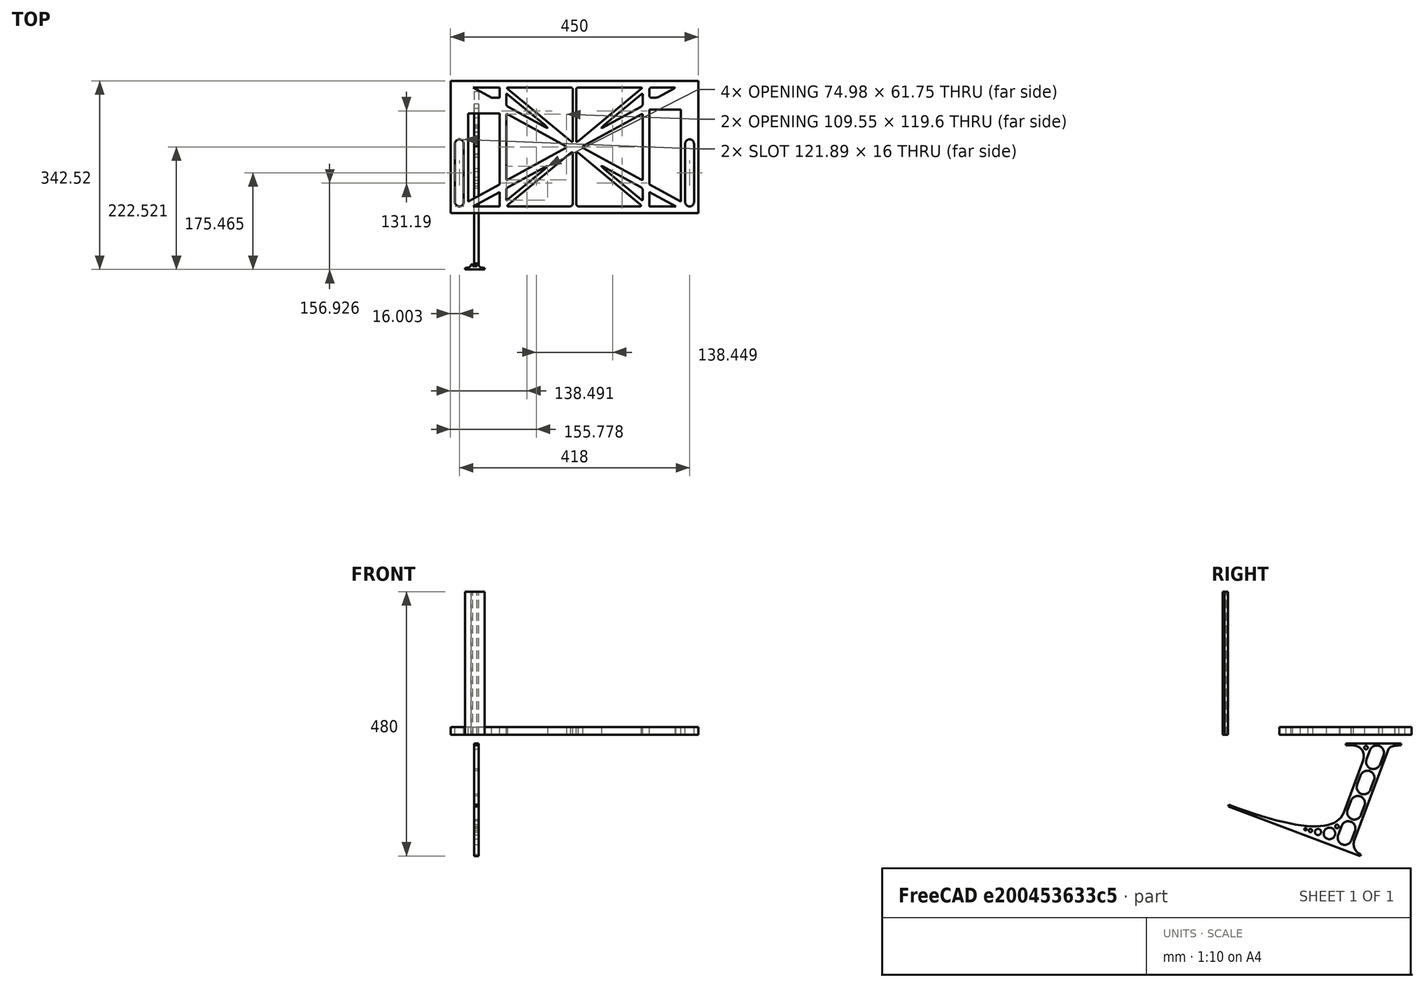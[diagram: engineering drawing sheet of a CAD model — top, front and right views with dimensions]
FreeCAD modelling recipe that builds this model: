
FCSTD DOCUMENT  (FreeCAD 0.19R0.19.2)
Label: laptopStand106
License: All rights reserved
LicenseURL: http://en.wikipedia.org/wiki/All_rights_reserved
objects: Sketcher::SketchObject×3, Part::Extrusion×3
note: 6 computed .brp shape members not serialized (recipe doc carries the construction recipe); baked Part::Feature solids carry a one-line shape summary decoded from their .brp

FEATURE [Sketcher::SketchObject] Sketch
  FullyConstrained = true
  sketch-geometry (288):
    g0: LineSegment StartX=-10.9272 StartY=-82.7794 StartZ=0 EndX=46.0728 EndY=-51.4823 EndZ=0
    g1: LineSegment StartX=366.073 StartY=-91.7794 StartZ=0 EndX=318.073 EndY=-65.424 EndZ=0
    g2: LineSegment StartX=-10.9272 StartY=77.3346 StartZ=0 EndX=-10.9272 EndY=-82.7794 EndZ=0
    g3: LineSegment StartX=-1.92719 StartY=-91.7794 StartZ=0 EndX=46.0728 EndY=-91.7794 EndZ=0
    g4: LineSegment StartX=318.073 StartY=-65.424 StartZ=0 EndX=318.073 EndY=-91.7794 EndZ=0
    g5: LineSegment StartX=318.073 StartY=-91.7794 StartZ=0 EndX=366.073 EndY=-91.7794 EndZ=0
    g6: LineSegment StartX=46.0728 StartY=-65.424 StartZ=0 EndX=-1.92719 EndY=-91.7794 EndZ=0
    g7: LineSegment StartX=46.0728 StartY=-65.424 StartZ=0 EndX=46.0728 EndY=-91.7794 EndZ=0
    g8: LineSegment StartX=46.0728 StartY=77.3346 StartZ=0 EndX=46.0728 EndY=-51.4823 EndZ=0
    g9: LineSegment StartX=-42.9272 StartY=136.221 StartZ=0 EndX=-42.9272 EndY=-103.779 EndZ=0
    g10: LineSegment StartX=407.073 StartY=136.221 StartZ=0 EndX=407.073 EndY=-103.779 EndZ=0
    g11: ArcOfCircle CenterX=-26.9272 CenterY=22.1087 CenterZ=0 NormalX=0 NormalY=0 NormalZ=1 AngleXU=0 Radius=8 StartAngle=1e-16 EndAngle=3.14159
    g12: ArcOfCircle CenterX=-26.9272 CenterY=-83.7794 CenterZ=0 NormalX=0 NormalY=0 NormalZ=1 AngleXU=0 Radius=8 StartAngle=3.14159 EndAngle=6.28319
    g13: LineSegment StartX=-34.9272 StartY=22.1087 StartZ=0 EndX=-34.9272 EndY=-83.7794 EndZ=0
    g14: LineSegment StartX=-18.9272 StartY=22.1087 StartZ=0 EndX=-18.9272 EndY=-83.7794 EndZ=0
    g15: ArcOfCircle CenterX=391.073 CenterY=22.1087 CenterZ=0 NormalX=0 NormalY=0 NormalZ=1 AngleXU=0 Radius=8 StartAngle=-4.4e-15 EndAngle=3.14159
    g16: LineSegment StartX=399.073 StartY=22.1087 StartZ=0 EndX=399.073 EndY=-83.7794 EndZ=0
    g17: LineSegment StartX=383.073 StartY=22.1087 StartZ=0 EndX=383.073 EndY=-83.7794 EndZ=0
    g18: ArcOfCircle CenterX=391.073 CenterY=-83.7794 CenterZ=0 NormalX=0 NormalY=0 NormalZ=1 AngleXU=0 Radius=8 StartAngle=3.14159 EndAngle=6.28319
    g19: Circle CenterX=175.022 CenterY=27.0628 CenterZ=0 NormalX=0 NormalY=0 NormalZ=1 AngleXU=0 Radius=1
    g20: Circle CenterX=179.022 CenterY=24.8665 CenterZ=0 NormalX=0 NormalY=0 NormalZ=1 AngleXU=0 Radius=1
    g21: Circle CenterX=179.022 CenterY=27.0628 CenterZ=0 NormalX=0 NormalY=0 NormalZ=1 AngleXU=0 Radius=1
    g22: BSplineCurve PolesCount=3 KnotsCount=2 Degree=2 IsPeriodic=0
    g23: GeomPoint X=175.022 Y=27.0628 Z=0
    g24: GeomPoint X=179.022 Y=27.0628 Z=0
    g25: Circle CenterX=189.124 CenterY=27.0628 CenterZ=0 NormalX=0 NormalY=0 NormalZ=1 AngleXU=0 Radius=1
    g26: Circle CenterX=185.124 CenterY=24.8665 CenterZ=0 NormalX=0 NormalY=0 NormalZ=1 AngleXU=0 Radius=1
    g27: Circle CenterX=185.124 CenterY=27.0628 CenterZ=0 NormalX=0 NormalY=0 NormalZ=1 AngleXU=0 Radius=1
    g28: BSplineCurve PolesCount=3 KnotsCount=2 Degree=2 IsPeriodic=0
    g29: GeomPoint X=189.124 Y=27.0628 Z=0
    g30: GeomPoint X=185.124 Y=27.0628 Z=0
    g31: Circle CenterX=175.022 CenterY=5.37834 CenterZ=0 NormalX=0 NormalY=0 NormalZ=1 AngleXU=0 Radius=1
    g32: Circle CenterX=179.022 CenterY=7.57463 CenterZ=0 NormalX=0 NormalY=0 NormalZ=1 AngleXU=0 Radius=1
    g33: Circle CenterX=179.022 CenterY=5.34704 CenterZ=0 NormalX=0 NormalY=0 NormalZ=1 AngleXU=0 Radius=1
    g34: BSplineCurve PolesCount=3 KnotsCount=2 Degree=2 IsPeriodic=0
    g35: GeomPoint X=175.022 Y=5.37834 Z=0
    g36: GeomPoint X=179.022 Y=5.34704 Z=0
    g37: Circle CenterX=189.124 CenterY=5.37834 CenterZ=0 NormalX=0 NormalY=0 NormalZ=1 AngleXU=0 Radius=1
    g38: Circle CenterX=185.124 CenterY=7.57463 CenterZ=0 NormalX=0 NormalY=0 NormalZ=1 AngleXU=0 Radius=1
    g39: Circle CenterX=185.124 CenterY=5.34704 CenterZ=0 NormalX=0 NormalY=0 NormalZ=1 AngleXU=0 Radius=1
    g40: BSplineCurve PolesCount=3 KnotsCount=2 Degree=2 IsPeriodic=0
    g41: GeomPoint X=189.124 Y=5.37834 Z=0
    g42: GeomPoint X=185.124 Y=5.34704 Z=0
    g43: Circle CenterX=165.871 CenterY=18.1458 CenterZ=0 NormalX=0 NormalY=0 NormalZ=1 AngleXU=0 Radius=1
    g44: Circle CenterX=169.377 CenterY=16.2206 CenterZ=0 NormalX=0 NormalY=0 NormalZ=1 AngleXU=0 Radius=1
    g45: Circle CenterX=165.871 CenterY=14.2954 CenterZ=0 NormalX=0 NormalY=0 NormalZ=1 AngleXU=0 Radius=1
    g46: BSplineCurve PolesCount=3 KnotsCount=2 Degree=2 IsPeriodic=0
    g47: GeomPoint X=165.871 Y=18.1458 Z=0
    g48: GeomPoint X=165.871 Y=14.2954 Z=0
    g49: Circle CenterX=198.275 CenterY=18.1458 CenterZ=0 NormalX=0 NormalY=0 NormalZ=1 AngleXU=0 Radius=1
    g50: Circle CenterX=194.768 CenterY=16.2206 CenterZ=0 NormalX=0 NormalY=0 NormalZ=1 AngleXU=0 Radius=1
    g51: Circle CenterX=198.275 CenterY=14.2954 CenterZ=0 NormalX=0 NormalY=0 NormalZ=1 AngleXU=0 Radius=1
    g52: BSplineCurve PolesCount=3 KnotsCount=2 Degree=2 IsPeriodic=0
    g53: GeomPoint X=198.275 Y=18.1458 Z=0
    g54: GeomPoint X=198.275 Y=14.2954 Z=0
    g55: LineSegment StartX=407.073 StartY=-103.779 StartZ=0 EndX=-42.9272 EndY=-103.779 EndZ=0
    g56: LineSegment StartX=407.073 StartY=136.221 StartZ=0 EndX=-42.9272 EndY=136.221 EndZ=0
    g57: LineSegment StartX=46.0728 StartY=77.3346 StartZ=0 EndX=-10.9272 EndY=77.3346 EndZ=0
    g58: LineSegment StartX=46.0728 StartY=105.865 StartZ=0 EndX=31.5028 EndY=105.865 EndZ=0
    g59: LineSegment StartX=46.0728 StartY=124.221 StartZ=0 EndX=46.0728 EndY=105.865 EndZ=0
    g60: LineSegment StartX=-1.92719 StartY=124.221 StartZ=0 EndX=31.5028 EndY=105.865 EndZ=0
    g61: LineSegment StartX=46.0728 StartY=124.221 StartZ=0 EndX=-1.92719 EndY=124.221 EndZ=0
    g62: Circle CenterX=125.607 CenterY=54.1951 CenterZ=0 NormalX=0 NormalY=0 NormalZ=1 AngleXU=0 Radius=1
    g63: Circle CenterX=139.632 CenterY=46.4944 CenterZ=0 NormalX=0 NormalY=0 NormalZ=1 AngleXU=0 Radius=1
    g64: Circle CenterX=127.326 CenterY=56.7187 CenterZ=0 NormalX=0 NormalY=0 NormalZ=1 AngleXU=0 Radius=1
    g65: BSplineCurve PolesCount=3 KnotsCount=2 Degree=2 IsPeriodic=0
    g66: GeomPoint X=125.607 Y=54.1951 Z=0
    g67: GeomPoint X=127.326 Y=56.7187 Z=0
    g68: Circle CenterX=236.821 CenterY=56.7187 CenterZ=0 NormalX=0 NormalY=0 NormalZ=1 AngleXU=0 Radius=1
    g69: Circle CenterX=224.513 CenterY=46.4944 CenterZ=0 NormalX=0 NormalY=0 NormalZ=1 AngleXU=0 Radius=1
    g70: Circle CenterX=238.538 CenterY=54.1951 CenterZ=0 NormalX=0 NormalY=0 NormalZ=1 AngleXU=0 Radius=1
    g71: BSplineCurve PolesCount=3 KnotsCount=2 Degree=2 IsPeriodic=0
    g72: GeomPoint X=236.821 Y=56.7187 Z=0
    g73: GeomPoint X=238.538 Y=54.1951 Z=0
    g74: Circle CenterX=238.538 CenterY=-21.7539 CenterZ=0 NormalX=0 NormalY=0 NormalZ=1 AngleXU=0 Radius=1
    g75: Circle CenterX=224.513 CenterY=-14.0532 CenterZ=0 NormalX=0 NormalY=0 NormalZ=1 AngleXU=0 Radius=1
    g76: Circle CenterX=236.821 CenterY=-24.2775 CenterZ=0 NormalX=0 NormalY=0 NormalZ=1 AngleXU=0 Radius=1
    g77: BSplineCurve PolesCount=3 KnotsCount=2 Degree=2 IsPeriodic=0
    g78: GeomPoint X=238.538 Y=-21.7539 Z=0
    g79: GeomPoint X=236.821 Y=-24.2775 Z=0
    g80: Circle CenterX=125.607 CenterY=-21.7539 CenterZ=0 NormalX=0 NormalY=0 NormalZ=1 AngleXU=0 Radius=1
    g81: Circle CenterX=139.632 CenterY=-14.0532 CenterZ=0 NormalX=0 NormalY=0 NormalZ=1 AngleXU=0 Radius=1
    g82: Circle CenterX=127.325 CenterY=-24.2775 CenterZ=0 NormalX=0 NormalY=0 NormalZ=1 AngleXU=0 Radius=1
    g83: BSplineCurve PolesCount=3 KnotsCount=2 Degree=2 IsPeriodic=0
    g84: GeomPoint X=125.607 Y=-21.7539 Z=0
    g85: GeomPoint X=127.325 Y=-24.2775 Z=0
    g86: Circle CenterX=302.996 CenterY=111.695 CenterZ=0 NormalX=0 NormalY=0 NormalZ=1 AngleXU=0 Radius=1
    g87: Circle CenterX=306.073 CenterY=114.251 CenterZ=0 NormalX=0 NormalY=0 NormalZ=1 AngleXU=0 Radius=1
    g88: Circle CenterX=306.073 CenterY=110.251 CenterZ=0 NormalX=0 NormalY=0 NormalZ=1 AngleXU=0 Radius=1
    g89: BSplineCurve PolesCount=3 KnotsCount=2 Degree=2 IsPeriodic=0
    g90: GeomPoint X=302.996 Y=111.695 Z=0
    g91: GeomPoint X=306.073 Y=110.251 Z=0
    g92: Circle CenterX=306.073 CenterY=95.2763 CenterZ=0 NormalX=0 NormalY=0 NormalZ=1 AngleXU=0 Radius=1
    g93: Circle CenterX=306.073 CenterY=91.2763 CenterZ=0 NormalX=0 NormalY=0 NormalZ=1 AngleXU=0 Radius=1
    g94: Circle CenterX=302.567 CenterY=89.3511 CenterZ=0 NormalX=0 NormalY=0 NormalZ=1 AngleXU=0 Radius=1
    g95: BSplineCurve PolesCount=3 KnotsCount=2 Degree=2 IsPeriodic=0
    g96: GeomPoint X=306.073 Y=95.2763 Z=0
    g97: GeomPoint X=302.567 Y=89.3511 Z=0
    g98: LineSegment StartX=306.073 StartY=110.251 StartZ=0 EndX=306.073 EndY=95.2763 EndZ=0
    g99: LineSegment StartX=302.996 StartY=111.695 StartZ=0 EndX=236.821 EndY=56.7187 EndZ=0
    g100: LineSegment StartX=238.538 StartY=54.1951 StartZ=0 EndX=302.567 EndY=89.3511 EndZ=0
    g101: Circle CenterX=61.1496 CenterY=111.695 CenterZ=0 NormalX=0 NormalY=0 NormalZ=1 AngleXU=0 Radius=1
    g102: Circle CenterX=58.0728 CenterY=114.251 CenterZ=0 NormalX=0 NormalY=0 NormalZ=1 AngleXU=0 Radius=1
    g103: Circle CenterX=58.0728 CenterY=110.251 CenterZ=0 NormalX=0 NormalY=0 NormalZ=1 AngleXU=0 Radius=1
    g104: BSplineCurve PolesCount=3 KnotsCount=2 Degree=2 IsPeriodic=0
    g105: GeomPoint X=61.1496 Y=111.695 Z=0
    g106: GeomPoint X=58.0728 Y=110.251 Z=0
    g107: Circle CenterX=61.5791 CenterY=89.3511 CenterZ=0 NormalX=0 NormalY=0 NormalZ=1 AngleXU=0 Radius=1
    g108: Circle CenterX=58.0728 CenterY=91.2763 CenterZ=0 NormalX=0 NormalY=0 NormalZ=1 AngleXU=0 Radius=1
    g109: Circle CenterX=58.0728 CenterY=95.2763 CenterZ=0 NormalX=0 NormalY=0 NormalZ=1 AngleXU=0 Radius=1
    g110: BSplineCurve PolesCount=3 KnotsCount=2 Degree=2 IsPeriodic=0
    g111: GeomPoint X=61.5791 Y=89.3511 Z=0
    g112: GeomPoint X=58.0728 Y=95.2763 Z=0
    g113: LineSegment StartX=58.0728 StartY=110.251 StartZ=0 EndX=58.0728 EndY=95.2763 EndZ=0
    g114: LineSegment StartX=61.1496 StartY=111.695 StartZ=0 EndX=127.326 EndY=56.7187 EndZ=0
    g115: LineSegment StartX=125.607 StartY=54.1951 StartZ=0 EndX=61.5791 EndY=89.3511 EndZ=0
    g116: Circle CenterX=61.5791 CenterY=-56.9099 CenterZ=0 NormalX=0 NormalY=0 NormalZ=1 AngleXU=0 Radius=1
    g117: Circle CenterX=58.0728 CenterY=-58.8351 CenterZ=0 NormalX=0 NormalY=0 NormalZ=1 AngleXU=0 Radius=1
    g118: Circle CenterX=58.0728 CenterY=-62.8351 CenterZ=0 NormalX=0 NormalY=0 NormalZ=1 AngleXU=0 Radius=1
    g119: BSplineCurve PolesCount=3 KnotsCount=2 Degree=2 IsPeriodic=0
    g120: GeomPoint X=61.5791 Y=-56.9099 Z=0
    g121: GeomPoint X=58.0728 Y=-62.8351 Z=0
    g122: Circle CenterX=58.0728 CenterY=-77.8102 CenterZ=0 NormalX=0 NormalY=0 NormalZ=1 AngleXU=0 Radius=1
    g123: Circle CenterX=58.0728 CenterY=-81.8102 CenterZ=0 NormalX=0 NormalY=0 NormalZ=1 AngleXU=0 Radius=1
    g124: Circle CenterX=61.1496 CenterY=-79.2541 CenterZ=0 NormalX=0 NormalY=0 NormalZ=1 AngleXU=0 Radius=1
    g125: BSplineCurve PolesCount=3 KnotsCount=2 Degree=2 IsPeriodic=0
    g126: GeomPoint X=58.0728 Y=-77.8102 Z=0
    g127: GeomPoint X=61.1496 Y=-79.2541 Z=0
    g128: LineSegment StartX=58.0728 StartY=-62.8351 StartZ=0 EndX=58.0728 EndY=-77.8102 EndZ=0
    g129: LineSegment StartX=61.1496 StartY=-79.2541 StartZ=0 EndX=127.325 EndY=-24.2775 EndZ=0
    g130: LineSegment StartX=125.607 StartY=-21.7539 StartZ=0 EndX=61.5791 EndY=-56.9099 EndZ=0
    g131: Circle CenterX=302.567 CenterY=-56.9099 CenterZ=0 NormalX=0 NormalY=0 NormalZ=1 AngleXU=0 Radius=1
    g132: Circle CenterX=306.073 CenterY=-58.8351 CenterZ=0 NormalX=0 NormalY=0 NormalZ=1 AngleXU=0 Radius=1
    g133: Circle CenterX=306.073 CenterY=-62.8351 CenterZ=0 NormalX=0 NormalY=0 NormalZ=1 AngleXU=0 Radius=1
    g134: BSplineCurve PolesCount=3 KnotsCount=2 Degree=2 IsPeriodic=0
    g135: GeomPoint X=302.567 Y=-56.9099 Z=0
    g136: GeomPoint X=306.073 Y=-62.8351 Z=0
    g137: Circle CenterX=302.996 CenterY=-79.2541 CenterZ=0 NormalX=0 NormalY=0 NormalZ=1 AngleXU=0 Radius=1
    g138: Circle CenterX=306.073 CenterY=-81.8102 CenterZ=0 NormalX=0 NormalY=0 NormalZ=1 AngleXU=0 Radius=1
    g139: Circle CenterX=306.073 CenterY=-77.8102 CenterZ=0 NormalX=0 NormalY=0 NormalZ=1 AngleXU=0 Radius=1
    g140: BSplineCurve PolesCount=3 KnotsCount=2 Degree=2 IsPeriodic=0
    g141: GeomPoint X=302.996 Y=-79.2541 Z=0
    g142: GeomPoint X=306.073 Y=-77.8102 Z=0
    g143: LineSegment StartX=306.073 StartY=-62.8351 StartZ=0 EndX=306.073 EndY=-77.8102 EndZ=0
    g144: LineSegment StartX=302.996 StartY=-79.2541 StartZ=0 EndX=236.821 EndY=-24.2775 EndZ=0
    g145: LineSegment StartX=238.538 StartY=-21.7539 StartZ=0 EndX=302.567 EndY=-56.9099 EndZ=0
    g146: Circle CenterX=61.6457 CenterY=-88.8112 CenterZ=0 NormalX=0 NormalY=0 NormalZ=1 AngleXU=0 Radius=1
    g147: Circle CenterX=58.0728 CenterY=-91.7794 CenterZ=0 NormalX=0 NormalY=0 NormalZ=1 AngleXU=0 Radius=1
    g148: Circle CenterX=63.9135 CenterY=-91.7794 CenterZ=0 NormalX=0 NormalY=0 NormalZ=1 AngleXU=0 Radius=1
    g149: BSplineCurve PolesCount=3 KnotsCount=2 Degree=2 IsPeriodic=0
    g150: GeomPoint X=61.6457 Y=-88.8112 Z=0
    g151: GeomPoint X=63.9135 Y=-91.7794 Z=0
    g152: Circle CenterX=179.022 CenterY=-85.8163 CenterZ=0 NormalX=0 NormalY=0 NormalZ=1 AngleXU=0 Radius=1
    g153: Circle CenterX=179.022 CenterY=-91.7794 CenterZ=0 NormalX=0 NormalY=0 NormalZ=1 AngleXU=0 Radius=1
    g154: Circle CenterX=171.895 CenterY=-91.7794 CenterZ=0 NormalX=0 NormalY=0 NormalZ=1 AngleXU=0 Radius=1
    g155: BSplineCurve PolesCount=3 KnotsCount=2 Degree=2 IsPeriodic=0
    g156: GeomPoint X=179.022 Y=-85.8163 Z=0
    g157: GeomPoint X=171.895 Y=-91.7794 Z=0
    g158: Circle CenterX=185.124 CenterY=-86.2028 CenterZ=0 NormalX=0 NormalY=0 NormalZ=1 AngleXU=0 Radius=1
    g159: Circle CenterX=185.124 CenterY=-91.7794 CenterZ=0 NormalX=0 NormalY=0 NormalZ=1 AngleXU=0 Radius=1
    g160: Circle CenterX=191.747 CenterY=-91.7794 CenterZ=0 NormalX=0 NormalY=0 NormalZ=1 AngleXU=0 Radius=1
    g161: BSplineCurve PolesCount=3 KnotsCount=2 Degree=2 IsPeriodic=0
    g162: GeomPoint X=185.124 Y=-86.2028 Z=0
    g163: GeomPoint X=191.747 Y=-91.7794 Z=0
    g164: Circle CenterX=299.888 CenterY=-86.6413 CenterZ=0 NormalX=0 NormalY=0 NormalZ=1 AngleXU=0 Radius=1
    g165: Circle CenterX=306.073 CenterY=-91.7794 CenterZ=0 NormalX=0 NormalY=0 NormalZ=1 AngleXU=0 Radius=1
    g166: Circle CenterX=298.776 CenterY=-91.7794 CenterZ=0 NormalX=0 NormalY=0 NormalZ=1 AngleXU=0 Radius=1
    g167: BSplineCurve PolesCount=3 KnotsCount=2 Degree=2 IsPeriodic=0
    g168: GeomPoint X=299.888 Y=-86.6413 Z=0
    g169: GeomPoint X=298.776 Y=-91.7794 Z=0
    g170: LineSegment StartX=189.124 StartY=5.37834 StartZ=0 EndX=299.888 EndY=-86.6413 EndZ=0
    g171: LineSegment StartX=298.776 StartY=-91.7794 StartZ=0 EndX=191.747 EndY=-91.7794 EndZ=0
    g172: LineSegment StartX=185.124 StartY=-86.2028 StartZ=0 EndX=185.124 EndY=5.34704 EndZ=0
    g173: LineSegment StartX=179.022 StartY=5.34704 StartZ=0 EndX=179.022 EndY=-85.8163 EndZ=0
    g174: LineSegment StartX=171.895 StartY=-91.7794 StartZ=0 EndX=63.9135 EndY=-91.7794 EndZ=0
    g175: LineSegment StartX=61.6457 StartY=-88.8112 StartZ=0 EndX=175.022 EndY=5.37834 EndZ=0
    g176: Circle CenterX=302.073 CenterY=124.221 CenterZ=0 NormalX=0 NormalY=0 NormalZ=1 AngleXU=0 Radius=1
    g177: Circle CenterX=306.073 CenterY=124.221 CenterZ=0 NormalX=0 NormalY=0 NormalZ=1 AngleXU=0 Radius=1
    g178: Circle CenterX=302.996 CenterY=121.665 CenterZ=0 NormalX=0 NormalY=0 NormalZ=1 AngleXU=0 Radius=1
    g179: BSplineCurve PolesCount=3 KnotsCount=2 Degree=2 IsPeriodic=0
    g180: GeomPoint X=302.073 Y=124.221 Z=0
    g181: GeomPoint X=302.996 Y=121.665 Z=0
    g182: Circle CenterX=189.124 CenterY=124.221 CenterZ=0 NormalX=0 NormalY=0 NormalZ=1 AngleXU=0 Radius=1
    g183: Circle CenterX=185.124 CenterY=124.221 CenterZ=0 NormalX=0 NormalY=0 NormalZ=1 AngleXU=0 Radius=1
    g184: Circle CenterX=185.124 CenterY=120.221 CenterZ=0 NormalX=0 NormalY=0 NormalZ=1 AngleXU=0 Radius=1
    g185: BSplineCurve PolesCount=3 KnotsCount=2 Degree=2 IsPeriodic=0
    g186: GeomPoint X=189.124 Y=124.221 Z=0
    g187: GeomPoint X=185.124 Y=120.221 Z=0
    g188: Circle CenterX=175.022 CenterY=124.221 CenterZ=0 NormalX=0 NormalY=0 NormalZ=1 AngleXU=0 Radius=1
    g189: Circle CenterX=179.022 CenterY=124.221 CenterZ=0 NormalX=0 NormalY=0 NormalZ=1 AngleXU=0 Radius=1
    g190: Circle CenterX=179.022 CenterY=120.221 CenterZ=0 NormalX=0 NormalY=0 NormalZ=1 AngleXU=0 Radius=1
    g191: BSplineCurve PolesCount=3 KnotsCount=2 Degree=2 IsPeriodic=0
    g192: GeomPoint X=175.022 Y=124.221 Z=0
    g193: GeomPoint X=179.022 Y=120.221 Z=0
    g194: Circle CenterX=62.0728 CenterY=124.221 CenterZ=0 NormalX=0 NormalY=0 NormalZ=1 AngleXU=0 Radius=1
    g195: Circle CenterX=58.0728 CenterY=124.221 CenterZ=0 NormalX=0 NormalY=0 NormalZ=1 AngleXU=0 Radius=1
    g196: Circle CenterX=61.1496 CenterY=121.665 CenterZ=0 NormalX=0 NormalY=0 NormalZ=1 AngleXU=0 Radius=1
    g197: BSplineCurve PolesCount=3 KnotsCount=2 Degree=2 IsPeriodic=0
    g198: GeomPoint X=62.0728 Y=124.221 Z=0
    g199: GeomPoint X=61.1496 Y=121.665 Z=0
    g200: LineSegment StartX=62.0728 StartY=124.221 StartZ=0 EndX=175.022 EndY=124.221 EndZ=0
    g201: LineSegment StartX=179.022 StartY=120.221 StartZ=0 EndX=179.022 EndY=27.0628 EndZ=0
    g202: LineSegment StartX=185.124 StartY=27.0628 StartZ=0 EndX=185.124 EndY=120.221 EndZ=0
    g203: LineSegment StartX=189.124 StartY=124.221 StartZ=0 EndX=302.073 EndY=124.221 EndZ=0
    g204: LineSegment StartX=302.996 StartY=121.665 StartZ=0 EndX=189.124 EndY=27.0628 EndZ=0
    g205: LineSegment StartX=175.022 StartY=27.0628 StartZ=0 EndX=61.1496 EndY=121.665 EndZ=0
    g206: Circle CenterX=61.5791 CenterY=75.4095 CenterZ=0 NormalX=0 NormalY=0 NormalZ=1 AngleXU=0 Radius=1
    g207: Circle CenterX=58.0728 CenterY=77.3346 CenterZ=0 NormalX=0 NormalY=0 NormalZ=1 AngleXU=0 Radius=1
    g208: Circle CenterX=58.0728 CenterY=73.3346 CenterZ=0 NormalX=0 NormalY=0 NormalZ=1 AngleXU=0 Radius=1
    g209: BSplineCurve PolesCount=3 KnotsCount=2 Degree=2 IsPeriodic=0
    g210: GeomPoint X=61.5791 Y=75.4095 Z=0
    g211: GeomPoint X=58.0728 Y=73.3346 Z=0
    g212: Circle CenterX=58.0728 CenterY=-40.8935 CenterZ=0 NormalX=0 NormalY=0 NormalZ=1 AngleXU=0 Radius=1
    g213: Circle CenterX=58.0728 CenterY=-44.8935 CenterZ=0 NormalX=0 NormalY=0 NormalZ=1 AngleXU=0 Radius=1
    g214: Circle CenterX=61.5791 CenterY=-42.9683 CenterZ=0 NormalX=0 NormalY=0 NormalZ=1 AngleXU=0 Radius=1
    g215: BSplineCurve PolesCount=3 KnotsCount=2 Degree=2 IsPeriodic=0
    g216: GeomPoint X=58.0728 Y=-40.8935 Z=0
    g217: GeomPoint X=61.5791 Y=-42.9683 Z=0
    g218: LineSegment StartX=61.5791 StartY=-42.9683 StartZ=0 EndX=165.871 EndY=14.2954 EndZ=0
    g219: LineSegment StartX=165.871 StartY=18.1458 StartZ=0 EndX=61.5791 EndY=75.4095 EndZ=0
    g220: LineSegment StartX=58.0728 StartY=73.3346 StartZ=0 EndX=58.0728 EndY=-40.8935 EndZ=0
    g221: Circle CenterX=302.567 CenterY=-42.9683 CenterZ=0 NormalX=0 NormalY=0 NormalZ=1 AngleXU=0 Radius=1
    g222: Circle CenterX=306.073 CenterY=-44.8935 CenterZ=0 NormalX=0 NormalY=0 NormalZ=1 AngleXU=0 Radius=1
    g223: Circle CenterX=306.073 CenterY=-40.8935 CenterZ=0 NormalX=0 NormalY=0 NormalZ=1 AngleXU=0 Radius=1
    g224: BSplineCurve PolesCount=3 KnotsCount=2 Degree=2 IsPeriodic=0
    g225: GeomPoint X=302.567 Y=-42.9683 Z=0
    g226: GeomPoint X=306.073 Y=-40.8935 Z=0
    g227: Circle CenterX=306.073 CenterY=73.3346 CenterZ=0 NormalX=0 NormalY=0 NormalZ=1 AngleXU=0 Radius=1
    g228: Circle CenterX=306.073 CenterY=77.3346 CenterZ=0 NormalX=0 NormalY=0 NormalZ=1 AngleXU=0 Radius=1
    g229: Circle CenterX=302.567 CenterY=75.4095 CenterZ=0 NormalX=0 NormalY=0 NormalZ=1 AngleXU=0 Radius=1
    g230: BSplineCurve PolesCount=3 KnotsCount=2 Degree=2 IsPeriodic=0
    g231: GeomPoint X=306.073 Y=73.3346 Z=0
    g232: GeomPoint X=302.567 Y=75.4095 Z=0
    g233: LineSegment StartX=302.567 StartY=-42.9683 StartZ=0 EndX=198.275 EndY=14.2954 EndZ=0
    g234: LineSegment StartX=198.275 StartY=18.1458 StartZ=0 EndX=302.567 EndY=75.4095 EndZ=0
    g235: LineSegment StartX=306.073 StartY=73.3346 StartZ=0 EndX=306.073 EndY=-40.8935 EndZ=0
    g236: LineSegment StartX=322.073 StartY=105.865 StartZ=0 EndX=328.643 EndY=105.865 EndZ=0
    g237: LineSegment StartX=318.073 StartY=120.221 StartZ=0 EndX=318.073 EndY=109.865 EndZ=0
    g238: LineSegment StartX=336.157 StartY=107.779 StartZ=0 EndX=362.567 EndY=122.294 EndZ=0
    g239: Circle CenterX=362.073 CenterY=124.221 CenterZ=0 NormalX=0 NormalY=0 NormalZ=1 AngleXU=0 Radius=1
    g240: Circle CenterX=366.073 CenterY=124.221 CenterZ=0 NormalX=0 NormalY=0 NormalZ=1 AngleXU=0 Radius=1
    g241: Circle CenterX=362.567 CenterY=122.294 CenterZ=0 NormalX=0 NormalY=0 NormalZ=1 AngleXU=0 Radius=1
    g242: BSplineCurve PolesCount=3 KnotsCount=2 Degree=2 IsPeriodic=0
    g243: GeomPoint X=362.073 Y=124.221 Z=0
    g244: GeomPoint X=362.567 Y=122.294 Z=0
    g245: Circle CenterX=322.073 CenterY=124.221 CenterZ=0 NormalX=0 NormalY=0 NormalZ=1 AngleXU=0 Radius=1
    g246: Circle CenterX=318.073 CenterY=124.221 CenterZ=0 NormalX=0 NormalY=0 NormalZ=1 AngleXU=0 Radius=1
    g247: Circle CenterX=318.073 CenterY=120.221 CenterZ=0 NormalX=0 NormalY=0 NormalZ=1 AngleXU=0 Radius=1
    g248: BSplineCurve PolesCount=3 KnotsCount=2 Degree=2 IsPeriodic=0
    g249: GeomPoint X=322.073 Y=124.221 Z=0
    g250: GeomPoint X=318.073 Y=120.221 Z=0
    g251: Circle CenterX=322.073 CenterY=105.865 CenterZ=0 NormalX=0 NormalY=0 NormalZ=1 AngleXU=0 Radius=1
    g252: Circle CenterX=318.073 CenterY=105.865 CenterZ=0 NormalX=0 NormalY=0 NormalZ=1 AngleXU=0 Radius=1
    g253: Circle CenterX=318.073 CenterY=109.865 CenterZ=0 NormalX=0 NormalY=0 NormalZ=1 AngleXU=0 Radius=1
    g254: BSplineCurve PolesCount=3 KnotsCount=2 Degree=2 IsPeriodic=0
    g255: GeomPoint X=322.073 Y=105.865 Z=0
    g256: GeomPoint X=318.073 Y=109.865 Z=0
    g257: Circle CenterX=336.157 CenterY=107.779 CenterZ=0 NormalX=0 NormalY=0 NormalZ=1 AngleXU=0 Radius=1
    g258: Circle CenterX=332.651 CenterY=105.853 CenterZ=0 NormalX=0 NormalY=0 NormalZ=1 AngleXU=0 Radius=1
    g259: Circle CenterX=328.643 CenterY=105.865 CenterZ=0 NormalX=0 NormalY=0 NormalZ=1 AngleXU=0 Radius=1
    g260: BSplineCurve PolesCount=3 KnotsCount=2 Degree=2 IsPeriodic=0
    g261: GeomPoint X=336.157 Y=107.779 Z=0
    g262: GeomPoint X=328.643 Y=105.865 Z=0
    g263: LineSegment StartX=322.073 StartY=124.221 StartZ=0 EndX=362.073 EndY=124.221 EndZ=0
    g264: Circle CenterX=371.567 CenterY=-80.8644 CenterZ=0 NormalX=0 NormalY=0 NormalZ=1 AngleXU=0 Radius=1
    g265: Circle CenterX=375.073 CenterY=-82.7896 CenterZ=0 NormalX=0 NormalY=0 NormalZ=1 AngleXU=0 Radius=1
    g266: Circle CenterX=375.073 CenterY=-78.7896 CenterZ=0 NormalX=0 NormalY=0 NormalZ=1 AngleXU=0 Radius=1
    g267: BSplineCurve PolesCount=3 KnotsCount=2 Degree=2 IsPeriodic=0
    g268: GeomPoint X=371.567 Y=-80.8644 Z=0
    g269: GeomPoint X=375.073 Y=-78.7896 Z=0
    g270: Circle CenterX=321.579 CenterY=-53.4075 CenterZ=0 NormalX=0 NormalY=0 NormalZ=1 AngleXU=0 Radius=1
    g271: Circle CenterX=318.073 CenterY=-51.4823 CenterZ=0 NormalX=0 NormalY=0 NormalZ=1 AngleXU=0 Radius=1
    g272: Circle CenterX=318.073 CenterY=-47.4823 CenterZ=0 NormalX=0 NormalY=0 NormalZ=1 AngleXU=0 Radius=1
    g273: BSplineCurve PolesCount=3 KnotsCount=2 Degree=2 IsPeriodic=0
    g274: GeomPoint X=321.579 Y=-53.4075 Z=0
    g275: GeomPoint X=318.073 Y=-47.4823 Z=0
    g276: Circle CenterX=318.073 CenterY=79.9235 CenterZ=0 NormalX=0 NormalY=0 NormalZ=1 AngleXU=0 Radius=1
    g277: Circle CenterX=318.073 CenterY=83.9235 CenterZ=0 NormalX=0 NormalY=0 NormalZ=1 AngleXU=0 Radius=1
    g278: Circle CenterX=322.073 CenterY=83.9235 CenterZ=0 NormalX=0 NormalY=0 NormalZ=1 AngleXU=0 Radius=1
    g279: BSplineCurve PolesCount=3 KnotsCount=2 Degree=2 IsPeriodic=0
    g280: GeomPoint X=318.073 Y=79.9235 Z=0
    g281: GeomPoint X=322.073 Y=83.9235 Z=0
    g282: Circle CenterX=375.073 CenterY=79.9235 CenterZ=0 NormalX=0 NormalY=0 NormalZ=1 AngleXU=0 Radius=1
    g283: Circle CenterX=375.073 CenterY=83.9235 CenterZ=0 NormalX=0 NormalY=0 NormalZ=1 AngleXU=0 Radius=1
    g284: Circle CenterX=371.073 CenterY=83.9235 CenterZ=0 NormalX=0 NormalY=0 NormalZ=1 AngleXU=0 Radius=1
    g285: BSplineCurve PolesCount=3 KnotsCount=2 Degree=2 IsPeriodic=0
    g286: GeomPoint X=375.073 Y=79.9235 Z=0
    g287: GeomPoint X=371.073 Y=83.9235 Z=0
  constraints (477):
    c: Horizontal(g3)
    c: Coincident(g4,g1)
    c: Coincident(g7,g6)
    c: Coincident(g0,g8)
    c: Block(g1)
    c: Block(g4)
    c: Block(g7)
    c: Block(g6)
    c: Block(g0)
    c: Block(g2)
    c: Block(g5)
    c: Block(g3)
    c: Vertical(g9)
    c: Vertical(g10)
    c: Block(g10)
    c: Block(g9)
    c: Tangent(g11,g14) = 1.5708
    c: Tangent(g11,g13) = -1.5708
    c: Tangent(g13,g12) = -1.5708
    c: Tangent(g14,g12) = 1.5708
    c: Vertical(g13)
    c: Equal(g11,g12)
    c: Block(g14)
    c: Block(g13)
    c: Tangent(g15,g16) = 1.5708
    c: Tangent(g16,g18) = 1.5708
    c: Equal(g15,g18)
    c: Coincident(g17,g15)
    c: Coincident(g17,g18)
    c: Block(g16)
    c: Block(g17)
    c: Weight(g19) = 1
    c: Equal(g19,g20)
    c: Equal(g19,g21)
    c: InternalAlignment(g19,g22)
    c: InternalAlignment(g20,g22)
    c: InternalAlignment(g21,g22)
    c: InternalAlignment(g23,g22)
    c: InternalAlignment(g24,g22)
    c: Weight(g25) = 1
    c: Equal(g25,g26)
    c: Equal(g25,g27)
    c: InternalAlignment(g25,g28)
    c: InternalAlignment(g26,g28)
    c: InternalAlignment(g27,g28)
    c: InternalAlignment(g29,g28)
    c: InternalAlignment(g30,g28)
    c: Block(g28)
    c: Block(g22)
    c: Weight(g31) = 1
    c: Equal(g31,g32)
    c: Equal(g31,g33)
    c: InternalAlignment(g31,g34)
    c: InternalAlignment(g32,g34)
    c: InternalAlignment(g33,g34)
    c: InternalAlignment(g35,g34)
    c: InternalAlignment(g36,g34)
    c: Weight(g37) = 1
    c: Equal(g37,g38)
    c: Equal(g37,g39)
    c: InternalAlignment(g37,g40)
    c: InternalAlignment(g38,g40)
    c: InternalAlignment(g39,g40)
    c: InternalAlignment(g41,g40)
    c: InternalAlignment(g42,g40)
    c: Block(g40)
    c: Block(g34)
    c: Weight(g43) = 1
    c: Equal(g43,g44)
    c: Equal(g43,g45)
    c: InternalAlignment(g43,g46)
    c: InternalAlignment(g44,g46)
    c: InternalAlignment(g45,g46)
    c: InternalAlignment(g47,g46)
    c: InternalAlignment(g48,g46)
    c: Weight(g49) = 1
    c: Equal(g49,g50)
    c: Equal(g49,g51)
    c: InternalAlignment(g49,g52)
    c: InternalAlignment(g50,g52)
    c: InternalAlignment(g51,g52)
    c: InternalAlignment(g53,g52)
    c: InternalAlignment(g54,g52)
    c: Block(g46)
    c: Block(g52)
    c: Coincident(g55,g10)
    c: Coincident(g55,g9)
    c: Horizontal(g55)
    c: Distance(g55) = 450
    c: Coincident(g56,g10)
    c: Coincident(g56,g9)
    c: Horizontal(g56)
    c: Horizontal(g57)
    c: Coincident(g8,g57)
    c: Horizontal(g58)
    c: Vertical(g59)
    c: Block(g59)
    c: Block(g58)
    c: Block(g57)
    c: Distance(g59) = 18.3554
    c: Coincident(g61,g59)
    c: Coincident(g61,g60)
    c: Horizontal(g61)
    c: Block(g61)
    c: Block(g60)
    c: Coincident(g58,g60)
    c: Coincident(g2,g57)
    c: Weight(g62) = 1
    c: Equal(g62,g63)
    c: Equal(g62,g64)
    c: InternalAlignment(g62,g65)
    c: InternalAlignment(g63,g65)
    c: InternalAlignment(g64,g65)
    c: InternalAlignment(g66,g65)
    c: InternalAlignment(g67,g65)
    c: Block(g65)
    c: Weight(g68) = 1
    c: Equal(g68,g69)
    c: Equal(g68,g70)
    c: InternalAlignment(g68,g71)
    c: InternalAlignment(g69,g71)
    c: InternalAlignment(g70,g71)
    c: InternalAlignment(g72,g71)
    c: InternalAlignment(g73,g71)
    c: Block(g71)
    c: Weight(g74) = 1
    c: Equal(g74,g75)
    c: Equal(g74,g76)
    c: InternalAlignment(g74,g77)
    c: InternalAlignment(g75,g77)
    c: InternalAlignment(g76,g77)
    c: InternalAlignment(g78,g77)
    c: InternalAlignment(g79,g77)
    c: Block(g77)
    c: Weight(g80) = 1
    c: Equal(g80,g81)
    c: Equal(g80,g82)
    c: InternalAlignment(g80,g83)
    c: InternalAlignment(g81,g83)
    c: InternalAlignment(g82,g83)
    c: InternalAlignment(g84,g83)
    c: InternalAlignment(g85,g83)
    c: Block(g83)
    c: Weight(g86) = 1
    c: Equal(g86,g87)
    c: Equal(g86,g88)
    c: InternalAlignment(g86,g89)
    c: InternalAlignment(g87,g89)
    c: InternalAlignment(g88,g89)
    c: InternalAlignment(g90,g89)
    c: InternalAlignment(g91,g89)
    c: Weight(g92) = 1
    c: Equal(g92,g93)
    c: Equal(g92,g94)
    c: InternalAlignment(g92,g95)
    c: InternalAlignment(g93,g95)
    c: InternalAlignment(g94,g95)
    c: InternalAlignment(g96,g95)
    c: InternalAlignment(g97,g95)
    c: Block(g89)
    c: Block(g95)
    c: Coincident(g98,g89)
    c: Coincident(g98,g95)
    c: Vertical(g98)
    c: Coincident(g99,g89)
    c: Coincident(g99,g71)
    c: Coincident(g100,g71)
    c: Coincident(g100,g95)
    c: Weight(g101) = 1
    c: Equal(g101,g102)
    c: Equal(g101,g103)
    c: InternalAlignment(g101,g104)
    c: InternalAlignment(g102,g104)
    c: InternalAlignment(g103,g104)
    c: InternalAlignment(g105,g104)
    c: InternalAlignment(g106,g104)
    c: Weight(g107) = 1
    c: Equal(g107,g108)
    c: Equal(g107,g109)
    c: InternalAlignment(g107,g110)
    c: InternalAlignment(g108,g110)
    c: InternalAlignment(g109,g110)
    c: InternalAlignment(g111,g110)
    c: InternalAlignment(g112,g110)
    c: Block(g104)
    c: Block(g110)
    c: Coincident(g113,g104)
    c: Coincident(g113,g110)
    c: Vertical(g113)
    c: Coincident(g114,g104)
    c: Coincident(g114,g65)
    c: Coincident(g115,g65)
    c: Coincident(g115,g110)
    c: Weight(g116) = 1
    c: Equal(g116,g117)
    c: Equal(g116,g118)
    c: InternalAlignment(g116,g119)
    c: InternalAlignment(g117,g119)
    c: InternalAlignment(g118,g119)
    c: InternalAlignment(g120,g119)
    c: InternalAlignment(g121,g119)
    c: Weight(g122) = 1
    c: Equal(g122,g123)
    c: Equal(g122,g124)
    c: InternalAlignment(g122,g125)
    c: InternalAlignment(g123,g125)
    c: InternalAlignment(g124,g125)
    c: InternalAlignment(g126,g125)
    c: InternalAlignment(g127,g125)
    c: Block(g119)
    c: Block(g125)
    c: Coincident(g128,g119)
    c: Coincident(g128,g125)
    c: Vertical(g128)
    c: Coincident(g129,g125)
    c: Coincident(g129,g83)
    c: Coincident(g130,g83)
    c: Coincident(g130,g119)
    c: Weight(g131) = 1
    c: Equal(g131,g132)
    c: Equal(g131,g133)
    c: InternalAlignment(g131,g134)
    c: InternalAlignment(g132,g134)
    c: InternalAlignment(g133,g134)
    c: InternalAlignment(g135,g134)
    c: InternalAlignment(g136,g134)
    c: Weight(g137) = 1
    c: Equal(g137,g138)
    c: Equal(g137,g139)
    c: InternalAlignment(g137,g140)
    c: InternalAlignment(g138,g140)
    c: InternalAlignment(g139,g140)
    c: InternalAlignment(g141,g140)
    c: InternalAlignment(g142,g140)
    c: Block(g134)
    c: Block(g140)
    c: Coincident(g143,g134)
    c: Coincident(g143,g140)
    c: Vertical(g143)
    c: Coincident(g144,g140)
    c: Coincident(g144,g77)
    c: Coincident(g145,g77)
    c: Coincident(g145,g134)
    c: Weight(g146) = 1
    c: Equal(g146,g147)
    c: Equal(g146,g148)
    c: InternalAlignment(g146,g149)
    c: InternalAlignment(g147,g149)
    c: InternalAlignment(g148,g149)
    c: InternalAlignment(g150,g149)
    c: InternalAlignment(g151,g149)
    c: Weight(g152) = 1
    c: Equal(g152,g153)
    c: Equal(g152,g154)
    c: InternalAlignment(g152,g155)
    c: InternalAlignment(g153,g155)
    c: InternalAlignment(g154,g155)
    c: InternalAlignment(g156,g155)
    c: InternalAlignment(g157,g155)
    c: Weight(g158) = 1
    c: Equal(g158,g159)
    c: Equal(g158,g160)
    c: InternalAlignment(g158,g161)
    c: InternalAlignment(g159,g161)
    c: InternalAlignment(g160,g161)
    c: InternalAlignment(g162,g161)
    c: InternalAlignment(g163,g161)
    c: Weight(g164) = 1
    c: Equal(g164,g165)
    c: Equal(g164,g166)
    c: InternalAlignment(g164,g167)
    c: InternalAlignment(g165,g167)
    c: InternalAlignment(g166,g167)
    c: InternalAlignment(g168,g167)
    c: InternalAlignment(g169,g167)
    c: Block(g167)
    c: Block(g161)
    c: Block(g155)
    c: Block(g149)
    c: Coincident(g170,g40)
    c: Coincident(g170,g167)
    c: Coincident(g171,g167)
    c: Coincident(g171,g161)
    c: Horizontal(g171)
    c: Coincident(g172,g161)
    c: Coincident(g172,g40)
    c: Vertical(g172)
    c: Coincident(g173,g34)
    c: Coincident(g173,g155)
    c: Vertical(g173)
    c: Coincident(g174,g155)
    c: Coincident(g174,g149)
    c: Horizontal(g174)
    c: Coincident(g175,g149)
    c: Coincident(g175,g34)
    c: Weight(g176) = 1
    c: Equal(g176,g177)
    c: Equal(g176,g178)
    c: InternalAlignment(g176,g179)
    c: InternalAlignment(g177,g179)
    c: InternalAlignment(g178,g179)
    c: InternalAlignment(g180,g179)
    c: InternalAlignment(g181,g179)
    c: Weight(g182) = 1
    c: Equal(g182,g183)
    c: Equal(g182,g184)
    c: InternalAlignment(g182,g185)
    c: InternalAlignment(g183,g185)
    c: InternalAlignment(g184,g185)
    c: InternalAlignment(g186,g185)
    c: InternalAlignment(g187,g185)
    c: Weight(g188) = 1
    c: Equal(g188,g189)
    c: Equal(g188,g190)
    c: InternalAlignment(g188,g191)
    c: InternalAlignment(g189,g191)
    c: InternalAlignment(g190,g191)
    c: InternalAlignment(g192,g191)
    c: InternalAlignment(g193,g191)
    c: Weight(g194) = 1
    c: Equal(g194,g195)
    c: Equal(g194,g196)
    c: InternalAlignment(g194,g197)
    c: InternalAlignment(g195,g197)
    c: InternalAlignment(g196,g197)
    c: InternalAlignment(g198,g197)
    c: InternalAlignment(g199,g197)
    c: Block(g197)
    c: Block(g191)
    c: Block(g185)
    c: Block(g179)
    c: Coincident(g200,g197)
    c: Coincident(g200,g191)
    c: Horizontal(g200)
    c: Coincident(g201,g191)
    c: Coincident(g201,g22)
    c: Vertical(g201)
    c: Coincident(g202,g28)
    c: Coincident(g202,g185)
    c: Vertical(g202)
    c: Coincident(g203,g185)
    c: Coincident(g203,g179)
    c: Horizontal(g203)
    c: Coincident(g204,g179)
    c: Coincident(g204,g28)
    c: Coincident(g205,g22)
    c: Weight(g206) = 1
    c: Equal(g206,g207)
    c: Equal(g206,g208)
    c: InternalAlignment(g206,g209)
    c: InternalAlignment(g207,g209)
    c: InternalAlignment(g208,g209)
    c: InternalAlignment(g210,g209)
    c: InternalAlignment(g211,g209)
    c: Weight(g212) = 1
    c: Equal(g212,g213)
    c: Equal(g212,g214)
    c: InternalAlignment(g212,g215)
    c: InternalAlignment(g213,g215)
    c: InternalAlignment(g214,g215)
    c: InternalAlignment(g216,g215)
    c: InternalAlignment(g217,g215)
    c: Block(g215)
    c: Block(g209)
    c: Coincident(g218,g215)
    c: Coincident(g218,g46)
    c: Coincident(g219,g46)
    c: Coincident(g219,g209)
    c: Coincident(g220,g209)
    c: Coincident(g220,g215)
    c: Vertical(g220)
    c: Weight(g221) = 1
    c: Equal(g221,g222)
    c: Equal(g221,g223)
    c: InternalAlignment(g221,g224)
    c: InternalAlignment(g222,g224)
    c: InternalAlignment(g223,g224)
    c: InternalAlignment(g225,g224)
    c: InternalAlignment(g226,g224)
    c: Weight(g227) = 1
    c: Equal(g227,g228)
    c: Equal(g227,g229)
    c: InternalAlignment(g227,g230)
    c: InternalAlignment(g228,g230)
    c: InternalAlignment(g229,g230)
    c: InternalAlignment(g231,g230)
    c: InternalAlignment(g232,g230)
    c: Block(g230)
    c: Block(g224)
    c: Coincident(g233,g224)
    c: Coincident(g233,g52)
    c: Coincident(g234,g52)
    c: Coincident(g234,g230)
    c: Coincident(g235,g230)
    c: Coincident(g235,g224)
    c: Vertical(g235)
    c: Horizontal(g236)
    c: Block(g236)
    c: Vertical(g237)
    c: Block(g237)
    c: Block(g238)
    c: Weight(g239) = 1
    c: Equal(g239,g240)
    c: Equal(g239,g241)
    c: InternalAlignment(g239,g242)
    c: InternalAlignment(g240,g242)
    c: InternalAlignment(g241,g242)
    c: InternalAlignment(g243,g242)
    c: InternalAlignment(g244,g242)
    c: Weight(g245) = 1
    c: Equal(g245,g246)
    c: Equal(g245,g247)
    c: InternalAlignment(g245,g248)
    c: InternalAlignment(g246,g248)
    c: InternalAlignment(g247,g248)
    c: InternalAlignment(g249,g248)
    c: InternalAlignment(g250,g248)
    c: Weight(g251) = 1
    c: Equal(g251,g252)
    c: Equal(g251,g253)
    c: InternalAlignment(g251,g254)
    c: InternalAlignment(g252,g254)
    c: InternalAlignment(g253,g254)
    c: InternalAlignment(g255,g254)
    c: InternalAlignment(g256,g254)
    c: Weight(g257) = 1
    c: Equal(g257,g258)
    c: Equal(g257,g259)
    c: InternalAlignment(g257,g260)
    c: InternalAlignment(g258,g260)
    c: InternalAlignment(g259,g260)
    c: InternalAlignment(g261,g260)
    c: InternalAlignment(g262,g260)
    c: Block(g242)
    c: Block(g248)
    c: Block(g254)
    c: Block(g260)
    c: Coincident(g263,g248)
    c: Coincident(g263,g242)
    c: Horizontal(g263)
    c: Block(g205)
    c: Weight(g264) = 1
    c: Equal(g264,g265)
    c: Equal(g264,g266)
    c: InternalAlignment(g264,g267)
    c: InternalAlignment(g265,g267)
    c: InternalAlignment(g266,g267)
    c: InternalAlignment(g268,g267)
    c: InternalAlignment(g269,g267)
    c: Weight(g270) = 1
    c: Equal(g270,g271)
    c: Equal(g270,g272)
    c: InternalAlignment(g270,g273)
    c: InternalAlignment(g271,g273)
    c: InternalAlignment(g272,g273)
    c: InternalAlignment(g274,g273)
    c: InternalAlignment(g275,g273)
    c: Weight(g276) = 1
    c: Equal(g276,g277)
    c: Equal(g276,g278)
    c: InternalAlignment(g276,g279)
    c: InternalAlignment(g277,g279)
    c: InternalAlignment(g278,g279)
    c: InternalAlignment(g280,g279)
    c: InternalAlignment(g281,g279)
    c: Weight(g282) = 1
    c: Equal(g282,g283)
    c: Equal(g282,g284)
    c: InternalAlignment(g282,g285)
    c: InternalAlignment(g283,g285)
    c: InternalAlignment(g284,g285)
    c: InternalAlignment(g286,g285)
    c: InternalAlignment(g287,g285)
    c: Block(g267)
    c: Block(g273)
    c: Block(g279)
    c: Block(g285)
FEATURE [Sketcher::SketchObject] Sketch001
  FullyConstrained = true
  MapMode = 4
  Placement = pos=(0,0,0) rot=(0.57735,0.57735,0.57735;2.0944rad)
  Support = -> [Sketch]
  sketch-geometry (46):
    g0: BSplineCurve PolesCount=3 KnotsCount=2 Degree=2 IsPeriodic=0
    g1: ArcOfCircle CenterX=73.1223 CenterY=-32.291 CenterZ=0 NormalX=0 NormalY=0 NormalZ=1 AngleXU=0 Radius=13 StartAngle=5.92268 EndAngle=9.06428
    g2: ArcOfCircle CenterX=66.7816 CenterY=-49.1439 CenterZ=0 NormalX=0 NormalY=0 NormalZ=1 AngleXU=0 Radius=13 StartAngle=2.78068 EndAngle=5.92131
    g3: ArcOfCircle CenterX=55.9263 CenterY=-78.1807 CenterZ=0 NormalX=0 NormalY=0 NormalZ=1 AngleXU=0 Radius=13 StartAngle=5.92268 EndAngle=9.06428
    g4: ArcOfCircle CenterX=49.5884 CenterY=-95.0342 CenterZ=0 NormalX=0 NormalY=0 NormalZ=1 AngleXU=0 Radius=13 StartAngle=2.78068 EndAngle=5.92131
    g5: ArcOfCircle CenterX=38.7206 CenterY=-124.067 CenterZ=0 NormalX=0 NormalY=0 NormalZ=1 AngleXU=0 Radius=13 StartAngle=5.92268 EndAngle=9.06428
    g6: ArcOfCircle CenterX=32.3875 CenterY=-140.92 CenterZ=0 NormalX=0 NormalY=0 NormalZ=1 AngleXU=0 Radius=13 StartAngle=2.78068 EndAngle=5.92131
    g7: ArcOfCircle CenterX=21.4715 CenterY=-169.934 CenterZ=0 NormalX=0 NormalY=0 NormalZ=1 AngleXU=0 Radius=13 StartAngle=5.92268 EndAngle=9.06428
    g8: ArcOfCircle CenterX=15.1336 CenterY=-186.787 CenterZ=0 NormalX=0 NormalY=0 NormalZ=1 AngleXU=0 Radius=13 StartAngle=2.78068 EndAngle=5.92131
    g9-g12: Circle x4 (B-spline internal-alignment scaffolding for g13; pole/knot coordinates omitted)
    g13: BSplineCurve PolesCount=4 KnotsCount=2 Degree=3 IsPeriodic=0
    g14: GeomPoint X=28.8094 Y=-19.0875 Z=0
    g15: GeomPoint X=47.0443 Y=-50.4712 Z=0
    g16: Circle CenterX=53.5586 CenterY=-23.2695 CenterZ=0 NormalX=0 NormalY=0 NormalZ=1 AngleXU=0 Radius=3.24518
    g17: Circle CenterX=-195.441 CenterY=-127.082 CenterZ=0 NormalX=0 NormalY=0 NormalZ=1 AngleXU=0 Radius=1
    g18: Circle CenterX=-8.24091 CenterY=-197.481 CenterZ=0 NormalX=0 NormalY=0 NormalZ=1 AngleXU=0 Radius=1
    g19: Circle CenterX=12.8789 CenterY=-141.321 CenterZ=0 NormalX=0 NormalY=0 NormalZ=1 AngleXU=0 Radius=1
    g20: BSplineCurve PolesCount=3 KnotsCount=2 Degree=2 IsPeriodic=0
    g21: GeomPoint X=-195.441 Y=-127.082 Z=0
    g22: GeomPoint X=12.8789 Y=-141.321 Z=0
    g23: Circle CenterX=-12.8016 CenterY=-179.036 CenterZ=0 NormalX=0 NormalY=0 NormalZ=1 AngleXU=0 Radius=10.5072
    g24: Circle CenterX=0.933922 CenterY=-166.43 CenterZ=0 NormalX=0 NormalY=0 NormalZ=1 AngleXU=0 Radius=3.26661
    g25: Circle CenterX=-33.5518 CenterY=-176.44 CenterZ=0 NormalX=0 NormalY=0 NormalZ=1 AngleXU=0 Radius=5.64388
    g26: Circle CenterX=-47.2366 CenterY=-173.859 CenterZ=0 NormalX=0 NormalY=0 NormalZ=1 AngleXU=0 Radius=3.01653
    g27: Circle CenterX=-56.2595 CenterY=-171.456 CenterZ=0 NormalX=0 NormalY=0 NormalZ=1 AngleXU=0 Radius=2.12826
    g28: ArcOfCircle CenterX=51.2151 CenterY=-198.473 CenterZ=0 NormalX=0 NormalY=0 NormalZ=1 AngleXU=0 Radius=20 StartAngle=2.78189 EndAngle=4.35269
    g29: LineSegment StartX=32.4951 StartY=-191.433 StartZ=0 EndX=94.6578 EndY=-26.1352 EndZ=0
    g30: LineSegment StartX=43.1192 StartY=-220.001 StartZ=0 EndX=-196.497 EndY=-129.89 EndZ=0
    g31: LineSegment StartX=43.1192 StartY=-220.001 StartZ=0 EndX=44.1752 EndY=-217.193 EndZ=0
    g32: LineSegment StartX=117.223 StartY=-19.0875 StartZ=0 EndX=117.223 EndY=-16.0875 EndZ=0
    g33: LineSegment StartX=117.223 StartY=-16.0875 StartZ=0 EndX=17.2232 EndY=-16.0875 EndZ=0
    g34: LineSegment StartX=17.2232 StartY=-16.0875 StartZ=0 EndX=17.2232 EndY=-19.0875 EndZ=0
    g35: LineSegment StartX=28.8094 StartY=-19.0875 StartZ=0 EndX=17.2232 EndY=-19.0875 EndZ=0
    g36: LineSegment StartX=47.0443 StartY=-50.4712 StartZ=0 EndX=12.8789 EndY=-141.321 EndZ=0
    g37: LineSegment StartX=-195.441 StartY=-127.082 StartZ=0 EndX=-196.497 EndY=-129.89 EndZ=0
    g38: LineSegment StartX=85.2866 StartY=-36.8766 StartZ=0 EndX=78.9396 EndY=-53.7463 EndZ=0
    g39: LineSegment StartX=60.9579 StartY=-27.7053 StartZ=0 EndX=54.6191 EndY=-44.5532 EndZ=0
    g40: LineSegment StartX=68.0907 StartY=-82.7664 StartZ=0 EndX=61.7465 EndY=-99.6365 EndZ=0
    g41: LineSegment StartX=43.7619 StartY=-73.595 StartZ=0 EndX=37.426 EndY=-90.4435 EndZ=0
    g42: LineSegment StartX=50.885 StartY=-128.652 StartZ=0 EndX=44.5456 EndY=-145.522 EndZ=0
    g43: LineSegment StartX=26.5562 StartY=-119.481 StartZ=0 EndX=20.2251 EndY=-136.329 EndZ=0
    g44: LineSegment StartX=9.3071 StartY=-165.349 StartZ=0 EndX=2.97115 EndY=-182.197 EndZ=0
    g45: LineSegment StartX=33.6358 StartY=-174.52 StartZ=0 EndX=27.2917 EndY=-191.39 EndZ=0
  constraints (71):
    c: Block(g0)
    c: Block(g1)
    c: Block(g2)
    c: Block(g4)
    c: Block(g3)
    c: Block(g6)
    c: Block(g5)
    c: Block(g8)
    c: Block(g7)
    c: Weight(g9) = 1
    c: Equal(g9,g10)
    c: Equal(g9,g11)
    c: Equal(g9,g12)
    c: InternalAlignment(g9-g12 -> g13) x4
    c: InternalAlignment(g14,g13)
    c: InternalAlignment(g15,g13)
    c: Block(g16)
    c: Weight(g17) = 1
    c: Equal(g17,g18)
    c: Equal(g17,g19)
    c: InternalAlignment(g17,g20)
    c: InternalAlignment(g18,g20)
    c: InternalAlignment(g19,g20)
    c: InternalAlignment(g21,g20)
    c: InternalAlignment(g22,g20)
    c: Block(g20)
    c: Block(g23)
    c: Block(g24)
    c: Block(g25)
    c: Block(g26)
    c: Block(g27)
    c: Block(g28)
    c: Coincident(g29,g28)
    c: Coincident(g29,g0)
    c: Block(g13)
    c: Coincident(g31,g30)
    c: Coincident(g31,g28)
    c: Block(g31)
    c: Coincident(g32,g0)
    c: Vertical(g32)
    c: Coincident(g33,g32)
    c: Horizontal(g33)
    c: Coincident(g34,g33)
    c: Vertical(g34)
    c: Block(g33)
    c: Coincident(g35,g13)
    c: Coincident(g35,g34)
    c: Horizontal(g35)
    c: Coincident(g36,g13)
    c: Coincident(g36,g20)
    c: Coincident(g37,g20)
    c: Coincident(g37,g30)
    c: Block(g30)
    c: Coincident(g38,g1)
    c: Coincident(g38,g2)
    c: Coincident(g39,g1)
    c: Coincident(g39,g2)
    c: Coincident(g40,g3)
    c: Coincident(g40,g4)
    c: Coincident(g41,g3)
    c: Coincident(g41,g4)
    c: Coincident(g42,g5)
    c: Coincident(g42,g6)
    c: Coincident(g43,g5)
    c: Coincident(g43,g6)
    c: Coincident(g44,g7)
    c: Coincident(g44,g8)
    c: Coincident(g45,g7)
    c: Coincident(g45,g8)
    c: Distance(g30) = 256
    c: Distance(g33) = 100
FEATURE [Part::Extrusion] Extrude002
  Base = -> Sketch001
  Dir = (1,0,0)
  DirMode = 2
  FaceMakerClass = Part::FaceMakerBullseye
  LengthFwd = 8
  LengthRev = 0
  Solid = true
  Symmetric = false
FEATURE [Sketcher::SketchObject] Sketch002
  FullyConstrained = true
  sketch-geometry (20):
    g0: LineSegment StartX=-2.77179 StartY=-200.304 StartZ=0 EndX=5.22821 EndY=-200.304 EndZ=0
    g1: LineSegment StartX=5.22821 StartY=-200.304 StartZ=0 EndX=5.22821 EndY=-197.304 EndZ=0
    g2: LineSegment StartX=-2.77179 StartY=-200.304 StartZ=0 EndX=-2.77179 EndY=-197.304 EndZ=0
    g3: LineSegment StartX=5.22821 StartY=-197.304 StartZ=0 EndX=8.22821 EndY=-197.304 EndZ=0
    g4: LineSegment StartX=-2.77179 StartY=-197.304 StartZ=0 EndX=-5.77179 EndY=-197.304 EndZ=0
    g5: LineSegment StartX=19.2282 StartY=-203.304 StartZ=0 EndX=19.2282 EndY=-206.304 EndZ=0
    g6: LineSegment StartX=-16.7718 StartY=-203.304 StartZ=0 EndX=-16.7718 EndY=-206.304 EndZ=0
    g7: LineSegment StartX=-16.7718 StartY=-206.304 StartZ=0 EndX=19.2282 EndY=-206.304 EndZ=0
    g8: Circle CenterX=-16.7718 CenterY=-203.304 CenterZ=0 NormalX=0 NormalY=0 NormalZ=1 AngleXU=0 Radius=1
    g9: Circle CenterX=-5.77179 CenterY=-203.304 CenterZ=0 NormalX=0 NormalY=0 NormalZ=1 AngleXU=0 Radius=1
    g10: Circle CenterX=-5.77179 CenterY=-197.304 CenterZ=0 NormalX=0 NormalY=0 NormalZ=1 AngleXU=0 Radius=1
    g11: BSplineCurve PolesCount=3 KnotsCount=2 Degree=2 IsPeriodic=0
    g12: GeomPoint X=-16.7718 Y=-203.304 Z=0
    g13: GeomPoint X=-5.77179 Y=-197.304 Z=0
    g14: Circle CenterX=19.2282 CenterY=-203.304 CenterZ=0 NormalX=0 NormalY=0 NormalZ=1 AngleXU=0 Radius=1
    g15: Circle CenterX=8.22821 CenterY=-203.304 CenterZ=0 NormalX=0 NormalY=0 NormalZ=1 AngleXU=0 Radius=1
    g16: Circle CenterX=8.22821 CenterY=-197.304 CenterZ=0 NormalX=0 NormalY=0 NormalZ=1 AngleXU=0 Radius=1
    g17: BSplineCurve PolesCount=3 KnotsCount=2 Degree=2 IsPeriodic=0
    g18: GeomPoint X=19.2282 Y=-203.304 Z=0
    g19: GeomPoint X=8.22821 Y=-197.304 Z=0
  constraints (41):
    c: Horizontal(g0)
    c: Distance(g0) = 8
    c: Coincident(g1,g0)
    c: Vertical(g1)
    c: Distance(g1) = 3
    c: Coincident(g2,g0)
    c: Vertical(g2)
    c: Distance(g2) = 3
    c: Coincident(g3,g1)
    c: Horizontal(g3)
    c: Distance(g3) = 3
    c: Coincident(g4,g2)
    c: Horizontal(g4)
    c: Distance(g4) = 3
    c: Vertical(g5)
    c: Vertical(g6)
    c: Coincident(g7,g6)
    c: Coincident(g7,g5)
    c: Weight(g8) = 1
    c: Equal(g8,g9)
    c: Equal(g8,g10)
    c: Coincident(g11,g4)
    c: InternalAlignment(g8,g11)
    c: InternalAlignment(g9,g11)
    c: InternalAlignment(g10,g11)
    c: InternalAlignment(g12,g11)
    c: InternalAlignment(g13,g11)
    c: Coincident(g17,g5)
    c: Weight(g14) = 1
    c: Equal(g14,g15)
    c: Equal(g14,g16)
    c: Coincident(g17,g3)
    c: InternalAlignment(g14,g17)
    c: InternalAlignment(g15,g17)
    c: InternalAlignment(g16,g17)
    c: InternalAlignment(g18,g17)
    c: InternalAlignment(g19,g17)
    c: Block(g7)
    c: Block(g17)
    c: Block(g11)
    c: Block(g6)
FEATURE [Part::Extrusion] Extrude003
  Base = -> Sketch002
  Dir = (0,0,1)
  DirMode = 2
  FaceMakerClass = Part::FaceMakerBullseye
  LengthFwd = 260
  LengthRev = 0
  Solid = true
  Symmetric = false
FEATURE [Part::Extrusion] Extrude
  Base = -> Sketch
  Dir = (0,0,1)
  DirMode = 2
  FaceMakerClass = Part::FaceMakerBullseye
  LengthFwd = 14
  LengthRev = 0
  Solid = true
  Symmetric = false
